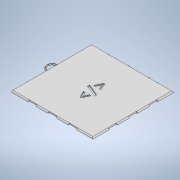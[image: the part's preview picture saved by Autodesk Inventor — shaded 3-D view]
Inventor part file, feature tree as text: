
AUTODESK INVENTOR PART (.ipt)
format: ipt  version: 2020 (Build 240168000, 168)  size: 214,528 bytes
history: native  units: in
note: dims shown in document units (in); Inventor stores cm internally (conversion verified against a paired STEP export)
features: fillet x2, sketch x2, extrude x1, emboss x1
ambient origin geometry x8: Origin, YZ Plane, XZ Plane, XY Plane, X Axis, Y Axis, Z Axis, Center Point
bodies: Solid1 (feature_tree)
feature tree (6):
  extrude  "Extrusion1"  Depth=3.937in
  fillet  "Fillet1"  Radius=0.9843in
  fillet  "Fillet2"  Radius=0.9843in
  emboss  "Emboss1"
  sketch  "Sketch1"  dims[d0=3.937in d1=3.937in d2=0.9843in d3=0.9843in]
  sketch  "Sketch2"  dims[d4=0.9843in d5=0.9843in d6=0.9843in d7=0.9843in d8=0.1969in d9=0.1969in d10=0.1969in d11=0.1969in d12=0.1969in d13=0.1969in d14=0.3937in d15=0.0591in d16=0.3937in d17=0.0591in d18=0.3937in d19=0.0591in d20=0.0591in d21=0.3937in d22=0.0591in d23=0.3937in d24=0.0591in d25=0.3937in d26=0.3937in d27=0.0591in d28=0.3937in d29=0.0591in d30=0.3937in d31=0.0591in d32=0.0591in d33=0.0in d34=0.0591in d35=0.2756in d36=0.0787in d37=0.0315in d38=0.0591in d39=0.0in]
